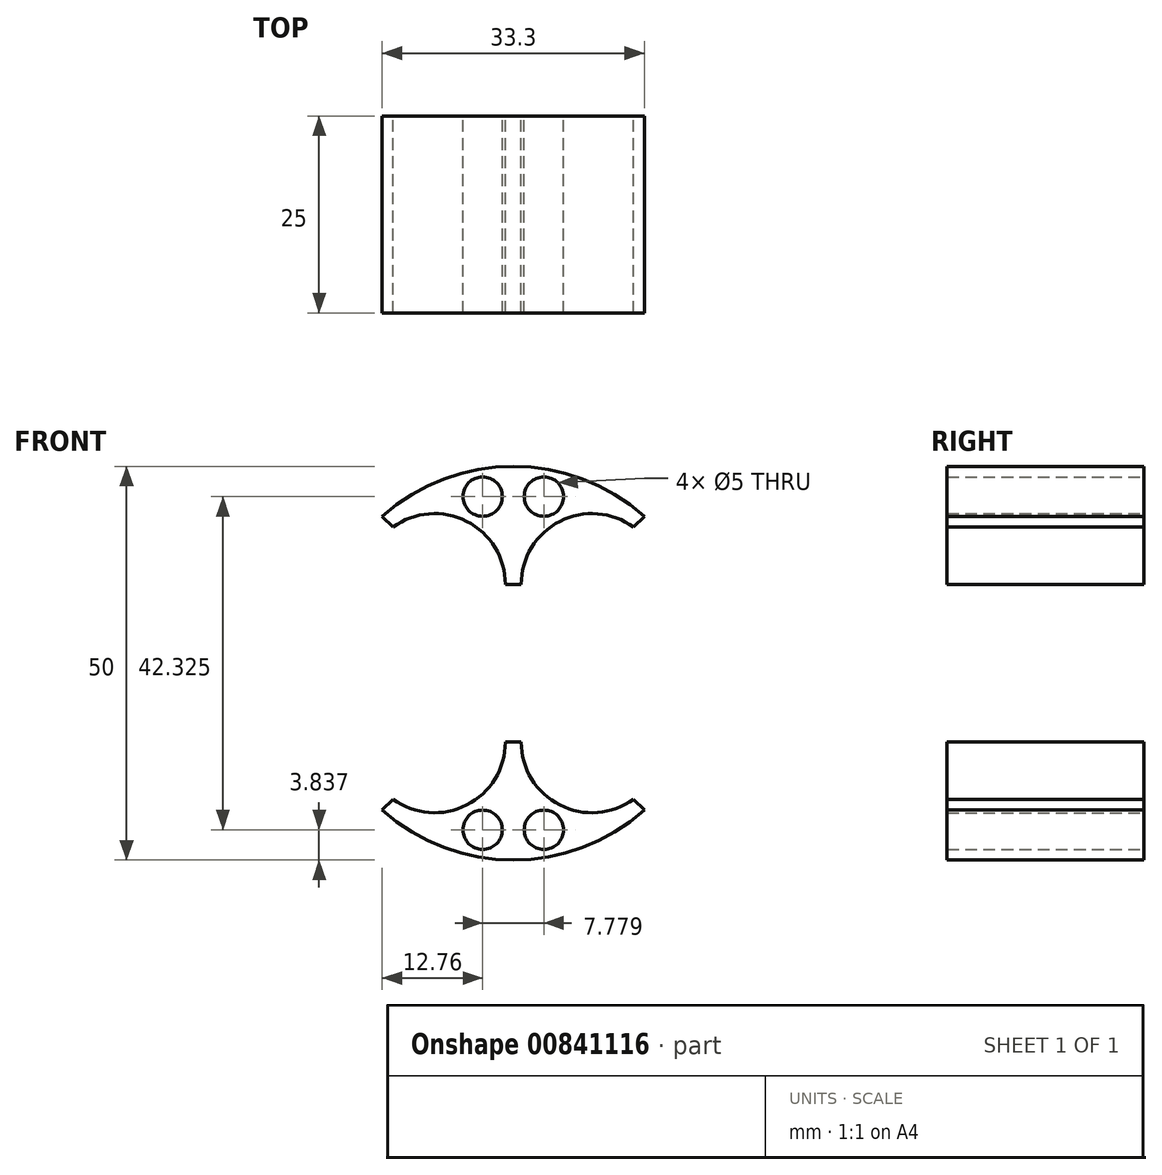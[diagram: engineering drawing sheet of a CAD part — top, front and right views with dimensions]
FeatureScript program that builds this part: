
annotation { "Feature Type Name" : "Feature", "Feature Type Description" : "" }
export const myFeature = defineFeature(function(context is Context, id is Id, definition is map)
    precondition{}
    {
        {
            var Q0;
            Q0=qCreatedBy(makeId("Front.planeOp"),FACE);
            var sketch = newSketch(context, id + "F0", { "sketchPlane" : qUnion([Q0])});
            skCircle(sketch, "E0", {"center": v(0, 0) * mm, "radius": 25 * mm});
            skSolve(sketch);
        }
        {
            var Q0;
            Q0=makeQuery(id+"F0.imprint","IMPRINT",FACE,{"disambiguationData":[TD([[makeQuery(id+"F0.imprint","IMPRINT",EDGE,{"derivedFrom":sQuery(id+"F0.wireOp",EDGE,"E0")}),1.0]])]});
            extrude(context, id + "F1", {"entities" : qUnion([Q0]), "depth" : 25 * mm, "offsetDistance" : 25 * mm});
        }
        {
            var Q0;
            Q0=qCreatedBy(makeId("Front.planeOp"),FACE);
            var sketch = newSketch(context, id + "F2", { "sketchPlane" : qUnion([Q0])});
            skCircle(sketch, "E1", {"center": v(10, 10) * mm, "radius": 9 * mm});
            skCircle(sketch, "E2.MirrorC", {"center": v(10, -10) * mm, "radius": 9 * mm});
            skCircle(sketch, "E3.MirrorC", {"center": v(-10, 10) * mm, "radius": 9 * mm});
            skCircle(sketch, "E4.MirrorC", {"center": v(-10, -10) * mm, "radius": 9 * mm});
            skSolve(sketch);
        }
        {
            var Q0;
            Q0 = qSketchRegion(id + "F2", true);
            extrude(context, id + "F3", {"entities" : qUnion([Q0]), "operationType" : NewBodyOperationType.REMOVE, "depth" : 27.8 * mm, "offsetDistance" : 25 * mm});
        }
        {
            var Q0;
            Q0=qCreatedBy(makeId("Front.planeOp"),FACE);
            var sketch = newSketch(context, id + "F4", { "sketchPlane" : qUnion([Q0])});
            skLineSegment(sketch, "E5.bottom", {"start": v(8, 10) * mm, "end": v(-8, 10) * mm});
            skLineSegment(sketch, "E5.top", {"start": v(8, -10) * mm, "end": v(-8, -10) * mm});
            skLineSegment(sketch, "E5.left", {"start": v(8, 10) * mm, "end": v(8, -10) * mm, "construction": true});
            skLineSegment(sketch, "E5.right", {"start": v(-8, 10) * mm, "end": v(-8, -10) * mm, "construction": true});
            skLineSegment(sketch, "E6", {"start": v(-8, 10) * mm, "end": v(-29.2, 31.2) * mm});
            skLineSegment(sketch, "E7", {"start": v(-29.2, 31.2) * mm, "end": v(-29.2, -31.2) * mm});
            skLineSegment(sketch, "E8", {"start": v(-29.2, -31.2) * mm, "end": v(-8, -10) * mm});
            skLineSegment(sketch, "E9", {"start": v(8, 10) * mm, "end": v(29.28, 31.28) * mm});
            skLineSegment(sketch, "E10", {"start": v(29.28, 31.28) * mm, "end": v(28.1, -30.1) * mm});
            skLineSegment(sketch, "E11", {"start": v(28.1, -30.1) * mm, "end": v(8, -10) * mm});
            skSolve(sketch);
        }
        {
            var Q0;
            Q0 = qSketchRegion(id + "F4", true);
            extrude(context, id + "F5", {"entities" : qUnion([Q0]), "operationType" : NewBodyOperationType.REMOVE, "depth" : 27.8 * mm, "offsetDistance" : 25 * mm});
        }
        {
            var Q0;
            Q0=qCreatedBy(makeId("Front.planeOp"),FACE);
            var sketch = newSketch(context, id + "F6", { "sketchPlane" : qUnion([Q0])});
            skCircle(sketch, "E12", {"center": v(-3.89, 21.16) * mm, "radius": 2.5 * mm});
            skCircle(sketch, "E13.MirrorC", {"center": v(3.89, 21.16) * mm, "radius": 2.5 * mm});
            skCircle(sketch, "E14.MirrorC", {"center": v(3.89, -21.16) * mm, "radius": 2.5 * mm});
            skCircle(sketch, "E15.MirrorC", {"center": v(-3.89, -21.16) * mm, "radius": 2.5 * mm});
            skSolve(sketch);
        }
        {
            var Q0;
            Q0 = qSketchRegion(id + "F6", true);
            extrude(context, id + "F7", {"entities" : qUnion([Q0]), "operationType" : NewBodyOperationType.REMOVE, "depth" : 45.7 * mm, "offsetDistance" : 25 * mm});
        }
    });
